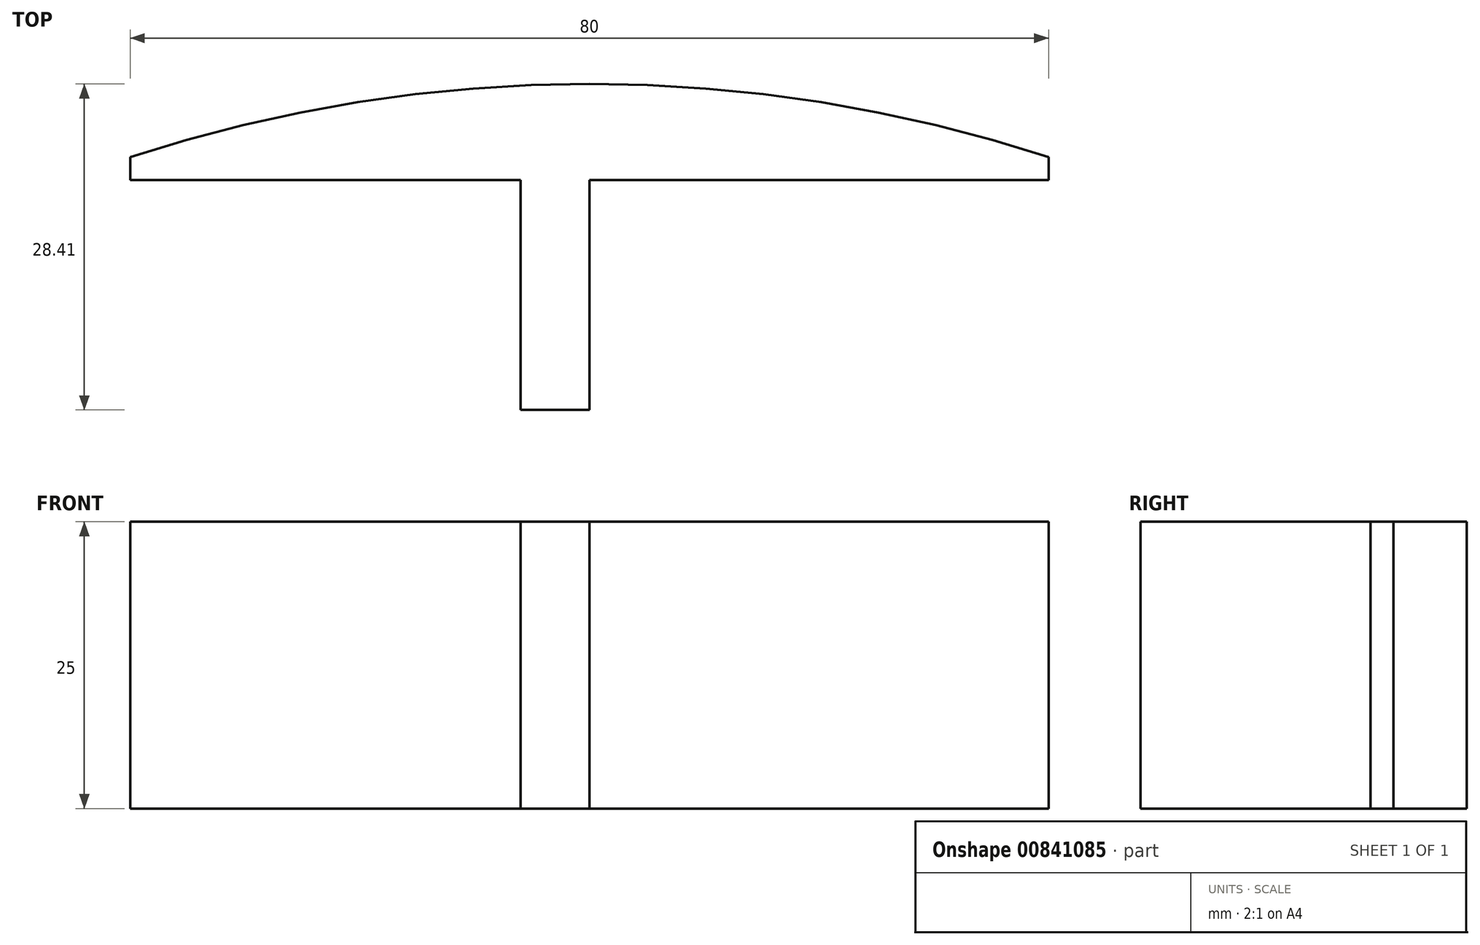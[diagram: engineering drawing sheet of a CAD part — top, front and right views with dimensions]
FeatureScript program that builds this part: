
annotation { "Feature Type Name" : "Feature", "Feature Type Description" : "" }
export const myFeature = defineFeature(function(context is Context, id is Id, definition is map)
    precondition{}
    {
        {
            var Q0;
            Q0=qCreatedBy(makeId("Top.planeOp"),FACE);
            var sketch = newSketch(context, id + "F0", { "sketchPlane" : qUnion([Q0])});
            skArc(sketch, "E0", {"start": v(40, 0) * mm, "mid": v(0, 6.37) * mm, "end": v(-40, 0) * mm});
            skLineSegment(sketch, "E1", {"start": v(-40, 0) * mm, "end": v(-40, -2) * mm});
            skLineSegment(sketch, "E2", {"start": v(-40, -2) * mm, "end": v(-6, -2) * mm});
            skLineSegment(sketch, "E3", {"start": v(-6, -2) * mm, "end": v(-6, -22.04) * mm});
            skLineSegment(sketch, "E4", {"start": v(-6, -22.04) * mm, "end": v(0, -22.04) * mm});
            skLineSegment(sketch, "E5", {"start": v(0, -22.04) * mm, "end": v(0, -2) * mm});
            skLineSegment(sketch, "E6", {"start": v(0, -2) * mm, "end": v(40, -2) * mm});
            skLineSegment(sketch, "E7", {"start": v(40, -2) * mm, "end": v(40, 0) * mm});
            skSolve(sketch);
        }
        {
            var Q0;
            Q0 = qSketchRegion(id + "F0", true);
            extrude(context, id + "F1", {"entities" : qUnion([Q0]), "depth" : 25 * mm, "offsetDistance" : 25 * mm});
        }
    });
